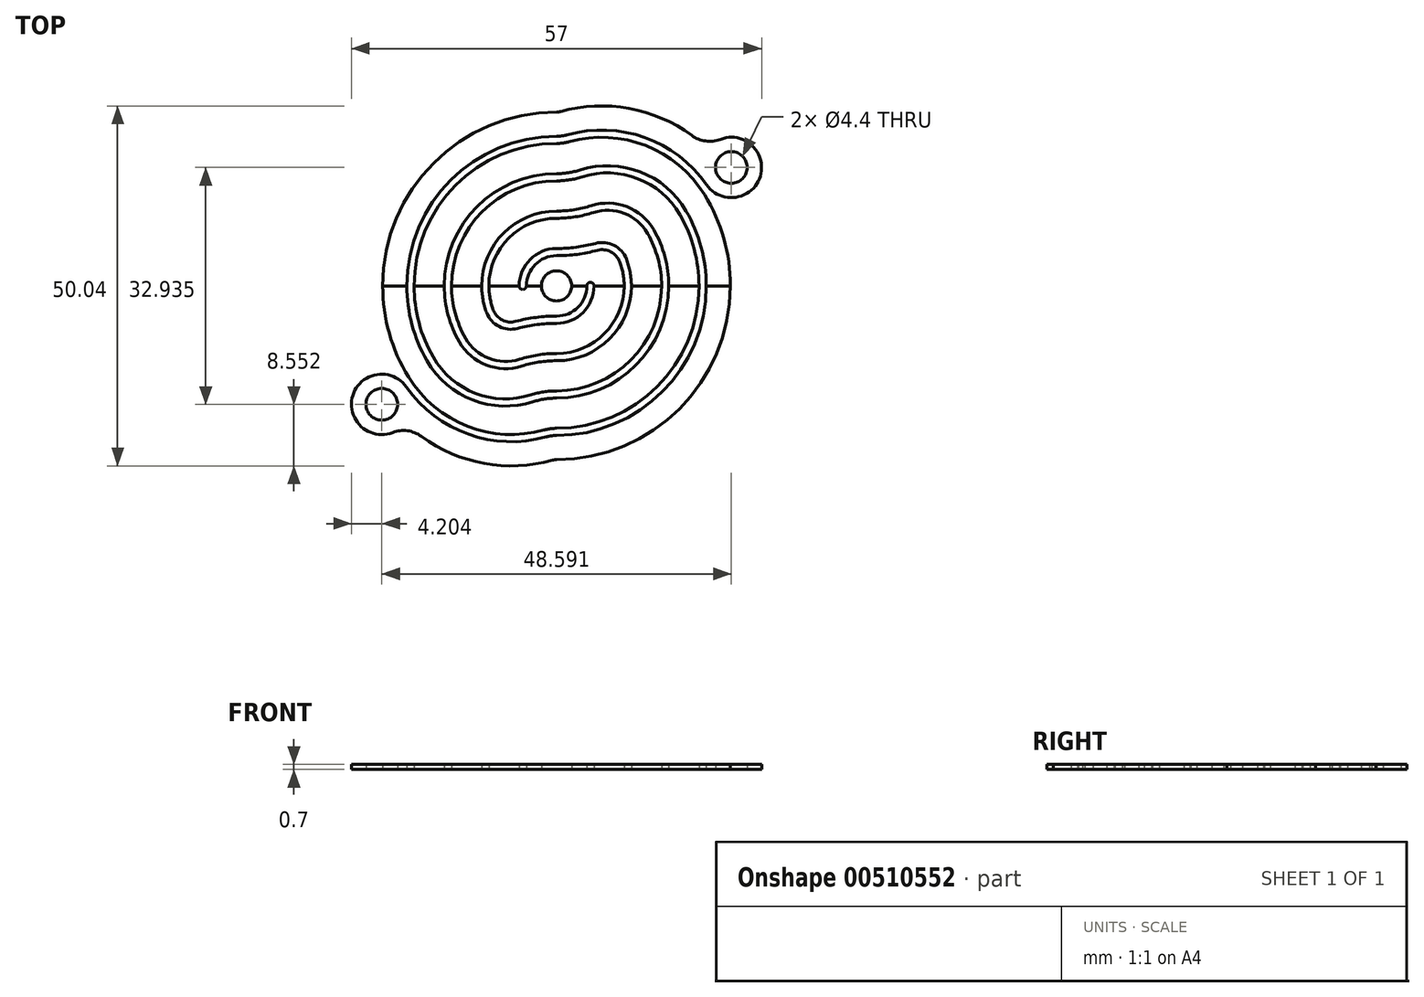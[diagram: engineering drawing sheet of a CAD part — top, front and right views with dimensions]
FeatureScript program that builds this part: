
annotation { "Feature Type Name" : "Feature", "Feature Type Description" : "" }
export const myFeature = defineFeature(function(context is Context, id is Id, definition is map)
    precondition{}
    {
        {
            var Q0;
            Q0=qCreatedBy(makeId("Top.planeOp"),FACE);
            var sketch = newSketch(context, id + "F0", { "sketchPlane" : qUnion([Q0])});
            skCircle(sketch, "E0", {"center": v(0, 0) * mm, "radius": 2.1 * mm, "construction": true});
            skArc(sketch, "E1.0", {"start": v(13.08, 8.5) * mm, "mid": v(12.8, 8.91) * mm, "end": v(12.51, 9.32) * mm, "construction": true});
            skArc(sketch, "E2.0", {"start": v(8.24, 18) * mm, "mid": v(-12.29, -15.52) * mm, "end": v(15.63, 12.15) * mm, "construction": true});
            skCircle(sketch, "E3.0", {"center": v(0, 0) * mm, "radius": 20.8 * mm, "construction": true});
            skArc(sketch, "E4.0", {"start": v(4.81, 23.68) * mm, "mid": v(-5.31, -23.57) * mm, "end": v(5.82, 23.45) * mm, "construction": true});
            skCircle(sketch, "E5.converted", {"center": v(0, 0) * mm, "radius": 4.2 * mm, "construction": true});
            skCircle(sketch, "E6.converted", {"center": v(0, 0) * mm, "radius": 5.2 * mm, "construction": true});
            skArc(sketch, "E7.converted", {"start": v(0, 9.4) * mm, "mid": v(-6.65, -6.65) * mm, "end": v(9.4, 0) * mm, "construction": true});
            skArc(sketch, "E8.converted", {"start": v(3.6, 9.75) * mm, "mid": v(3.58, 9.77) * mm, "end": v(3.55, 9.78) * mm, "construction": true});
            skArc(sketch, "E9", {"start": v(0, 14.6) * mm, "mid": v(-4.54, 13.88) * mm, "end": v(-8.63, 11.78) * mm, "construction": true});
            skArc(sketch, "E10", {"start": v(18.7, 16.59) * mm, "mid": v(18.69, 16.6) * mm, "end": v(18.67, 16.63) * mm, "construction": true});
            skCircle(sketch, "E11", {"center": v(0, 26.26) * mm, "radius": 24.16 * mm, "construction": true});
            skCircle(sketch, "E12", {"center": v(0, 26.26) * mm, "radius": 22.06 * mm, "construction": true});
            skCircle(sketch, "E13", {"center": v(0, 26.26) * mm, "radius": 21.06 * mm, "construction": true});
            skArc(sketch, "E14", {"start": v(-3.55, 9.78) * mm, "mid": v(2.73, 9.62) * mm, "end": v(8.63, 11.78) * mm, "construction": true});
            skCircle(sketch, "E15", {"center": v(0, 26.26) * mm, "radius": 11.66 * mm, "construction": true});
            skCircle(sketch, "E16", {"center": v(0, 26.26) * mm, "radius": 10.66 * mm, "construction": true});
            skArc(sketch, "E17", {"start": v(-5.82, 23.45) * mm, "mid": v(1.44, 19.96) * mm, "end": v(6.46, 26.26) * mm, "construction": true});
            skLineSegment(sketch, "E18", {"start": v(2.1, 0) * mm, "end": v(4.2, 0) * mm});
            skLineSegment(sketch, "E19", {"start": v(5.2, 0) * mm, "end": v(9.4, 0) * mm});
            skLineSegment(sketch, "E20", {"start": v(10.4, 0) * mm, "end": v(14.6, 0) * mm});
            skLineSegment(sketch, "E21", {"start": v(15.6, 0) * mm, "end": v(19.8, 0) * mm});
            skLineSegment(sketch, "E22", {"start": v(20.8, 0) * mm, "end": v(24.16, 0) * mm});
            skLineSegment(sketch, "E23", {"start": v(-2.1, 0) * mm, "end": v(-4.2, 0) * mm});
            skLineSegment(sketch, "E24", {"start": v(-5.2, 0) * mm, "end": v(-9.4, 0) * mm});
            skLineSegment(sketch, "E25", {"start": v(-10.4, 0) * mm, "end": v(-14.6, 0) * mm});
            skLineSegment(sketch, "E26", {"start": v(-15.6, 0) * mm, "end": v(-19.8, 0) * mm});
            skLineSegment(sketch, "E27", {"start": v(-20.8, 0) * mm, "end": v(-24.16, 0) * mm});
            skLineSegment(sketch, "E28", {"start": v(4.2, 0) * mm, "end": v(5.2, 0) * mm, "construction": true});
            skArc(sketch, "E29", {"start": v(5.2, 0) * mm, "mid": v(4.7, 0.5) * mm, "end": v(4.2, 0) * mm});
            skArc(sketch, "E30", {"start": v(0, 4.2) * mm, "mid": v(2.86, 4.39) * mm, "end": v(5.68, 4.94) * mm});
            skArc(sketch, "E31", {"start": v(8.78, 3.36) * mm, "mid": v(-5.33, -7.74) * mm, "end": v(0, 9.4) * mm, "construction": true});
            skPoint(sketch, "E32.visualSharp", {"position": v(7.59, 5.55) * mm});
            skArc(sketch, "E32.filletArc", {"start": v(8.78, 3.36) * mm, "mid": v(7.53, 4.75) * mm, "end": v(5.68, 4.94) * mm});
            skArc(sketch, "E33", {"start": v(0, 4.2) * mm, "mid": v(-2.97, 2.97) * mm, "end": v(-4.2, 0) * mm});
            skArc(sketch, "E34", {"start": v(2.1, 0) * mm, "mid": v(0, 2.1) * mm, "end": v(-2.1, 0) * mm});
            skArc(sketch, "E35", {"start": v(0, 5.2) * mm, "mid": v(-3.68, 3.68) * mm, "end": v(-5.2, 0) * mm});
            skArc(sketch, "E36", {"start": v(0, 5.2) * mm, "mid": v(2.73, 5.38) * mm, "end": v(5.42, 5.91) * mm});
            skArc(sketch, "E37", {"start": v(10.4, 0) * mm, "mid": v(10.19, 2.08) * mm, "end": v(9.57, 4.08) * mm, "construction": true});
            skPoint(sketch, "E38.visualSharp", {"position": v(7.92, 6.74) * mm});
            skArc(sketch, "E38.filletArc", {"start": v(9.71, 3.72) * mm, "mid": v(7.99, 5.64) * mm, "end": v(5.42, 5.91) * mm});
            skArc(sketch, "E39", {"start": v(0, 9.4) * mm, "mid": v(2.6, 9.6) * mm, "end": v(5.14, 10.2) * mm});
            skArc(sketch, "E40", {"start": v(14.6, 0) * mm, "mid": v(6.6, 13.02) * mm, "end": v(-8.63, 11.78) * mm, "construction": true});
            skPoint(sketch, "E41.visualSharp", {"position": v(-8.63, 11.78) * mm});
            skArc(sketch, "E42.trimOffspring", {"start": v(8.55, 5.92) * mm, "mid": v(8.24, 6.34) * mm, "end": v(7.92, 6.74) * mm, "construction": true});
            skArc(sketch, "E43", {"start": v(0, 9.4) * mm, "mid": v(-6.65, 6.65) * mm, "end": v(-9.4, 0) * mm});
            skArc(sketch, "E44.trimOffspring", {"start": v(0, 10.4) * mm, "mid": v(-5.73, -8.68) * mm, "end": v(9.57, 4.08) * mm, "construction": true});
            skArc(sketch, "E45.trimOffspring", {"start": v(0, 10.4) * mm, "mid": v(-7.35, -7.35) * mm, "end": v(10.4, 0) * mm});
            skArc(sketch, "E46", {"start": v(-8.63, 11.78) * mm, "mid": v(-6.6, -13.02) * mm, "end": v(14.6, 0) * mm, "construction": true});
            skArc(sketch, "E47.trimOffspring", {"start": v(0, 14.6) * mm, "mid": v(-10.42, -10.23) * mm, "end": v(14.6, -0.26) * mm, "construction": true});
            skArc(sketch, "E48", {"start": v(-8.63, 11.78) * mm, "mid": v(-8.18, 12.1) * mm, "end": v(-7.71, 12.4) * mm});
            skArc(sketch, "E49", {"start": v(15.6, 0) * mm, "mid": v(15.22, 3.4) * mm, "end": v(14.11, 6.65) * mm});
            skArc(sketch, "E50", {"start": v(-8.63, 11.78) * mm, "mid": v(-13.02, 6.6) * mm, "end": v(-14.6, 0) * mm});
            skLineSegment(sketch, "E51", {"start": v(0, 14.6) * mm, "end": v(0, 14.6) * mm});
            skArc(sketch, "E52", {"start": v(19.8, 0) * mm, "mid": v(17.94, 8.38) * mm, "end": v(12.7, 15.18) * mm, "construction": true});
            skPoint(sketch, "E53.visualSharp", {"position": v(8.24, 18) * mm});
            skArc(sketch, "E54.trimOffspring", {"start": v(13.08, 8.5) * mm, "mid": v(12.8, 8.91) * mm, "end": v(12.51, 9.32) * mm});
            skArc(sketch, "E55.trimOffspring", {"start": v(8.66, 12.97) * mm, "mid": v(6.24, 14.3) * mm, "end": v(3.62, 15.18) * mm, "construction": true});
            skArc(sketch, "E56.trimOffspring", {"start": v(0, 15.6) * mm, "mid": v(-11.03, -11.03) * mm, "end": v(15.6, 0) * mm, "construction": true});
            skArc(sketch, "E57.trimOffspring", {"start": v(0, 15.6) * mm, "mid": v(-8.84, -12.85) * mm, "end": v(14.57, 5.58) * mm, "construction": true});
            skArc(sketch, "E58", {"start": v(9.4, 0) * mm, "mid": v(9.24, 1.7) * mm, "end": v(8.78, 3.36) * mm});
            skArc(sketch, "E59", {"start": v(10.4, 0) * mm, "mid": v(10.23, 1.9) * mm, "end": v(9.71, 3.72) * mm});
            skArc(sketch, "E60", {"start": v(-9.71, 12.48) * mm, "mid": v(-2.56, 9.6) * mm, "end": v(5.14, 10.2) * mm, "construction": true});
            skArc(sketch, "E61", {"start": v(14.6, 0) * mm, "mid": v(14.1, 3.78) * mm, "end": v(12.65, 7.3) * mm});
            skPoint(sketch, "E62.visualSharp", {"position": v(8.63, 11.78) * mm});
            skArc(sketch, "E62.filletArc", {"start": v(12.65, 7.3) * mm, "mid": v(9.4, 10.07) * mm, "end": v(5.14, 10.2) * mm});
            skArc(sketch, "E63.trimOffspring", {"start": v(8.63, 11.78) * mm, "mid": v(10.88, 13.38) * mm, "end": v(12.83, 15.32) * mm, "construction": true});
            skArc(sketch, "E64", {"start": v(0, 14.6) * mm, "mid": v(-4.01, 14.04) * mm, "end": v(-7.71, 12.4) * mm});
            skArc(sketch, "E65", {"start": v(0, 15.6) * mm, "mid": v(-11.03, 11.03) * mm, "end": v(-15.6, 0) * mm});
            skArc(sketch, "E66", {"start": v(0, 14.6) * mm, "mid": v(1.8, 14.74) * mm, "end": v(3.55, 15.15) * mm});
            skArc(sketch, "E67", {"start": v(15.6, 0) * mm, "mid": v(15.07, 4.04) * mm, "end": v(13.51, 7.8) * mm});
            skCircle(sketch, "E68", {"center": v(0, 26.26) * mm, "radius": 15.86 * mm, "construction": true});
            skArc(sketch, "E69", {"start": v(0, 10.4) * mm, "mid": v(2.44, 10.59) * mm, "end": v(4.83, 11.15) * mm});
            skPoint(sketch, "E70.visualSharp", {"position": v(8.66, 12.97) * mm});
            skArc(sketch, "E70.filletArc", {"start": v(13.51, 7.8) * mm, "mid": v(9.76, 11) * mm, "end": v(4.83, 11.15) * mm});
            skArc(sketch, "E71", {"start": v(19.8, 0) * mm, "mid": v(19.13, 5.12) * mm, "end": v(17.15, 9.9) * mm});
            skArc(sketch, "E72.filletArc", {"start": v(17.15, 9.9) * mm, "mid": v(11.28, 14.92) * mm, "end": v(3.55, 15.15) * mm});
            skArc(sketch, "E73", {"start": v(0, 15.6) * mm, "mid": v(1.64, 15.73) * mm, "end": v(3.25, 16.1) * mm});
            skArc(sketch, "E74", {"start": v(20.8, 0) * mm, "mid": v(20.1, 5.38) * mm, "end": v(18.02, 10.4) * mm});
            skPoint(sketch, "E75.visualSharp", {"position": v(8, 19.2) * mm});
            skArc(sketch, "E75.filletArc", {"start": v(18.02, 10.4) * mm, "mid": v(11.64, 15.86) * mm, "end": v(3.25, 16.1) * mm});
            skArc(sketch, "E76", {"start": v(0, 19.8) * mm, "mid": v(-14, 14) * mm, "end": v(-19.8, 0) * mm});
            skArc(sketch, "E77", {"start": v(0, 19.8) * mm, "mid": v(1.58, 32.52) * mm, "end": v(-3.06, 20.57) * mm, "construction": true});
            skArc(sketch, "E78.trimOffspring", {"start": v(12.7, 15.18) * mm, "mid": v(12.41, 15.42) * mm, "end": v(12.11, 15.66) * mm, "construction": true});
            skArc(sketch, "E79.trimOffspring", {"start": v(17.38, 9.48) * mm, "mid": v(16.56, 10.85) * mm, "end": v(15.63, 12.15) * mm, "construction": true});
            skArc(sketch, "E80", {"start": v(24.16, 0) * mm, "mid": v(23.25, 6.58) * mm, "end": v(20.57, 12.67) * mm});
            skPoint(sketch, "E81.visualSharp", {"position": v(5.82, 23.45) * mm});
            skArc(sketch, "E82.trimOffspring", {"start": v(12.83, 15.32) * mm, "mid": v(-2.11, 42.99) * mm, "end": v(-9.71, 12.48) * mm, "construction": true});
            skArc(sketch, "E83.trimOffspring", {"start": v(12.13, 14.55) * mm, "mid": v(12.49, 14.93) * mm, "end": v(12.83, 15.32) * mm, "construction": true});
            skArc(sketch, "E84", {"start": v(0, 20.8) * mm, "mid": v(-14.7, 14.7) * mm, "end": v(-20.8, 0) * mm});
            skArc(sketch, "E85", {"start": v(0, 24.16) * mm, "mid": v(-17.08, 17.08) * mm, "end": v(-24.16, 0) * mm});
            skArc(sketch, "E86", {"start": v(0, 20.8) * mm, "mid": v(0.74, 20.85) * mm, "end": v(1.47, 21) * mm});
            skArc(sketch, "E87", {"start": v(4.81, 23.68) * mm, "mid": v(5, 24.06) * mm, "end": v(5.16, 24.46) * mm});
            skArc(sketch, "E88", {"start": v(25, 0) * mm, "mid": v(23.36, 8.9) * mm, "end": v(18.67, 16.63) * mm});
            skPoint(sketch, "E89.first.point", {"position": v(0.76, -10.46) * mm});
            skCircle(sketch, "E90.converted", {"center": v(0, 26.26) * mm, "radius": 5.46 * mm, "construction": true});
            skArc(sketch, "E91", {"start": v(-3.06, 20.57) * mm, "mid": v(-0.71, 19.84) * mm, "end": v(1.74, 20.04) * mm});
            skArc(sketch, "E92.filletArc", {"start": v(20.57, 12.67) * mm, "mid": v(12.39, 19.5) * mm, "end": v(1.74, 20.04) * mm});
            skArc(sketch, "E93.trimOffspring", {"start": v(12.7, 15.18) * mm, "mid": v(-19.13, -5.09) * mm, "end": v(18.57, -6.86) * mm, "construction": true});
            skArc(sketch, "E94.0", {"start": v(20.85, 14.06) * mm, "mid": v(12.27, 20.62) * mm, "end": v(1.47, 21) * mm});
            skCircle(sketch, "E95.converted", {"center": v(0, 26.26) * mm, "radius": 2.1 * mm, "construction": true});
            skArc(sketch, "E96.0", {"start": v(22.5, 17.44) * mm, "mid": v(22.01, 18) * mm, "end": v(21.5, 18.54) * mm, "construction": true});
            skArc(sketch, "E97", {"start": v(0, 24.16) * mm, "mid": v(0.29, 24.18) * mm, "end": v(0.57, 24.24) * mm});
            skLineSegment(sketch, "E98", {"start": v(0, 0) * mm, "end": v(23.64, 15.94) * mm, "construction": true});
            skArc(sketch, "E99.trimOffspring", {"start": v(18.79, 20.92) * mm, "mid": v(10.06, 24.68) * mm, "end": v(0.57, 24.24) * mm});
            skArc(sketch, "E100", {"start": v(20.85, 14.06) * mm, "mid": v(28.31, 15.24) * mm, "end": v(22.78, 20.39) * mm});
            skCircle(sketch, "E101", {"center": v(24.3, 16.47) * mm, "radius": 2.2 * mm});
            skPoint(sketch, "E102.visualSharp", {"position": v(20.99, 19.06) * mm});
            skArc(sketch, "E102.filletArc", {"start": v(18.79, 20.92) * mm, "mid": v(20.72, 20.14) * mm, "end": v(22.78, 20.39) * mm});
            skSolve(sketch);
        }
        {
            var Q0;
            Q0=makeQuery(id+"F0.imprint","IMPRINT",FACE,{"disambiguationData":[TD([[makeQuery(id+"F0.imprint","IMPRINT",EDGE,{"derivedFrom":sQuery(id+"F0.wireOp",EDGE,"E24")}),-1.0]])]});
            var Q1;
            Q1=makeQuery(id+"F0.imprint","IMPRINT",FACE,{"disambiguationData":[TD([[makeQuery(id+"F0.imprint","IMPRINT",EDGE,{"derivedFrom":sQuery(id+"F0.wireOp",EDGE,"E18")}),1.0]])]});
            var Q2;
            {var subQ1=sQuery(id+"F0.wireOp",EDGE,"E21");Q2=makeQuery(id+"F0.imprint","IMPRINT",FACE,{"disambiguationData":[TD([[makeQuery(id+"F0.imprint","IMPRINT",EDGE,{"derivedFrom":subQ1}),1.0]])]});}
            var Q3;
            Q3=makeQuery(id+"F0.imprint","IMPRINT",FACE,{"disambiguationData":[TD([[makeQuery(id+"F0.imprint","IMPRINT",EDGE,{"derivedFrom":sQuery(id+"F0.wireOp",EDGE,"E22")}),1.0]])]});
            var Q4;
            {var subQ6=sQuery(id+"F0.wireOp",EDGE,"E27");Q4=makeQuery(id+"F0.imprint","IMPRINT",FACE,{"disambiguationData":[TD([[makeQuery(id+"F0.imprint","IMPRINT",EDGE,{"derivedFrom":subQ6}),-1.0]])]});}
            extrude(context, id + "F1", {"entities" : qUnion([Q0, Q1, Q2, Q3, Q4]), "depth" : .7 * mm, "offsetDistance" : 25 * mm});
        }
        {
            var Q0;
            Q0=makeQuery(id+"F1.opExtrude","SWEPT_BODY",BODY,{"disambiguationData":[OSD([sQuery(id+"F0.wireOp",EDGE,"E18"),sQuery(id+"F0.wireOp",EDGE,"E19"),sQuery(id+"F0.wireOp",EDGE,"E23"),sQuery(id+"F0.wireOp",EDGE,"E29"),sQuery(id+"F0.wireOp",EDGE,"E30"),sQuery(id+"F0.wireOp",EDGE,"E32.filletArc"),sQuery(id+"F0.wireOp",EDGE,"E33"),sQuery(id+"F0.wireOp",EDGE,"E34")])]});
            var Q1;
            Q1=makeQuery(id+"F1.opExtrude","SWEPT_BODY",BODY,{"disambiguationData":[OSD([sQuery(id+"F0.wireOp",EDGE,"E20"),sQuery(id+"F0.wireOp",EDGE,"E24"),sQuery(id+"F0.wireOp",EDGE,"E35"),sQuery(id+"F0.wireOp",EDGE,"E36"),sQuery(id+"F0.wireOp",EDGE,"E38.filletArc"),sQuery(id+"F0.wireOp",EDGE,"E39"),sQuery(id+"F0.wireOp",EDGE,"E43"),sQuery(id+"F0.wireOp",EDGE,"E59"),sQuery(id+"F0.wireOp",EDGE,"E61"),sQuery(id+"F0.wireOp",EDGE,"E62.filletArc")])]});
            var Q2;
            Q2=makeQuery(id+"F1.opExtrude","SWEPT_BODY",BODY,{"disambiguationData":[OSD([sQuery(id+"F0.wireOp",EDGE,"E21"),sQuery(id+"F0.wireOp",EDGE,"E25"),sQuery(id+"F0.wireOp",EDGE,"E45.trimOffspring"),sQuery(id+"F0.wireOp",EDGE,"E48"),sQuery(id+"F0.wireOp",EDGE,"E50"),sQuery(id+"F0.wireOp",EDGE,"E64"),sQuery(id+"F0.wireOp",EDGE,"E66"),sQuery(id+"F0.wireOp",EDGE,"E67"),sQuery(id+"F0.wireOp",EDGE,"E69"),sQuery(id+"F0.wireOp",EDGE,"E70.filletArc"),sQuery(id+"F0.wireOp",EDGE,"E71"),sQuery(id+"F0.wireOp",EDGE,"E72.filletArc")])]});
            var Q3;
            Q3=makeQuery(id+"F1.opExtrude","SWEPT_BODY",BODY,{"disambiguationData":[OSD([sQuery(id+"F0.wireOp",EDGE,"E22"),sQuery(id+"F0.wireOp",EDGE,"E26"),sQuery(id+"F0.wireOp",EDGE,"E65"),sQuery(id+"F0.wireOp",EDGE,"E73"),sQuery(id+"F0.wireOp",EDGE,"E74"),sQuery(id+"F0.wireOp",EDGE,"E75.filletArc"),sQuery(id+"F0.wireOp",EDGE,"E76"),sQuery(id+"F0.wireOp",EDGE,"E80"),sQuery(id+"F0.wireOp",EDGE,"E91"),sQuery(id+"F0.wireOp",EDGE,"E92.filletArc")])]});
            var Q4;
            Q4=makeQuery(id+"F1.opExtrude","SWEPT_BODY",BODY,{"disambiguationData":[OSD([sQuery(id+"F0.wireOp",EDGE,"E27"),sQuery(id+"F0.wireOp",EDGE,"E84"),sQuery(id+"F0.wireOp",EDGE,"E85"),sQuery(id+"F0.wireOp",EDGE,"E86"),sQuery(id+"F0.wireOp",EDGE,"E94.0"),sQuery(id+"F0.wireOp",EDGE,"E97"),sQuery(id+"F0.wireOp",EDGE,"9NUbP7Mr-0lKH-UUtn-VFz5-Uik6tJHT7edk"),sQuery(id+"F0.wireOp",EDGE,"E99.trimOffspring"),sQuery(id+"F0.wireOp",EDGE,"eKzqWYXa-ZtuT-rVpZ-CJWK-zkNVA6rLTH0m")])]});
            var Q5;
            Q5=sQuery(id+"F0.wireOp",EDGE,"E0");
            circularPattern(context, id + "F2", {"entities" : qUnion([Q0, Q1, Q2, Q3, Q4]), "axis" : qUnion([Q5]), "angle" : 180 * degree, "instanceCount" : 2, "equalSpace" : true});
        }
    });
